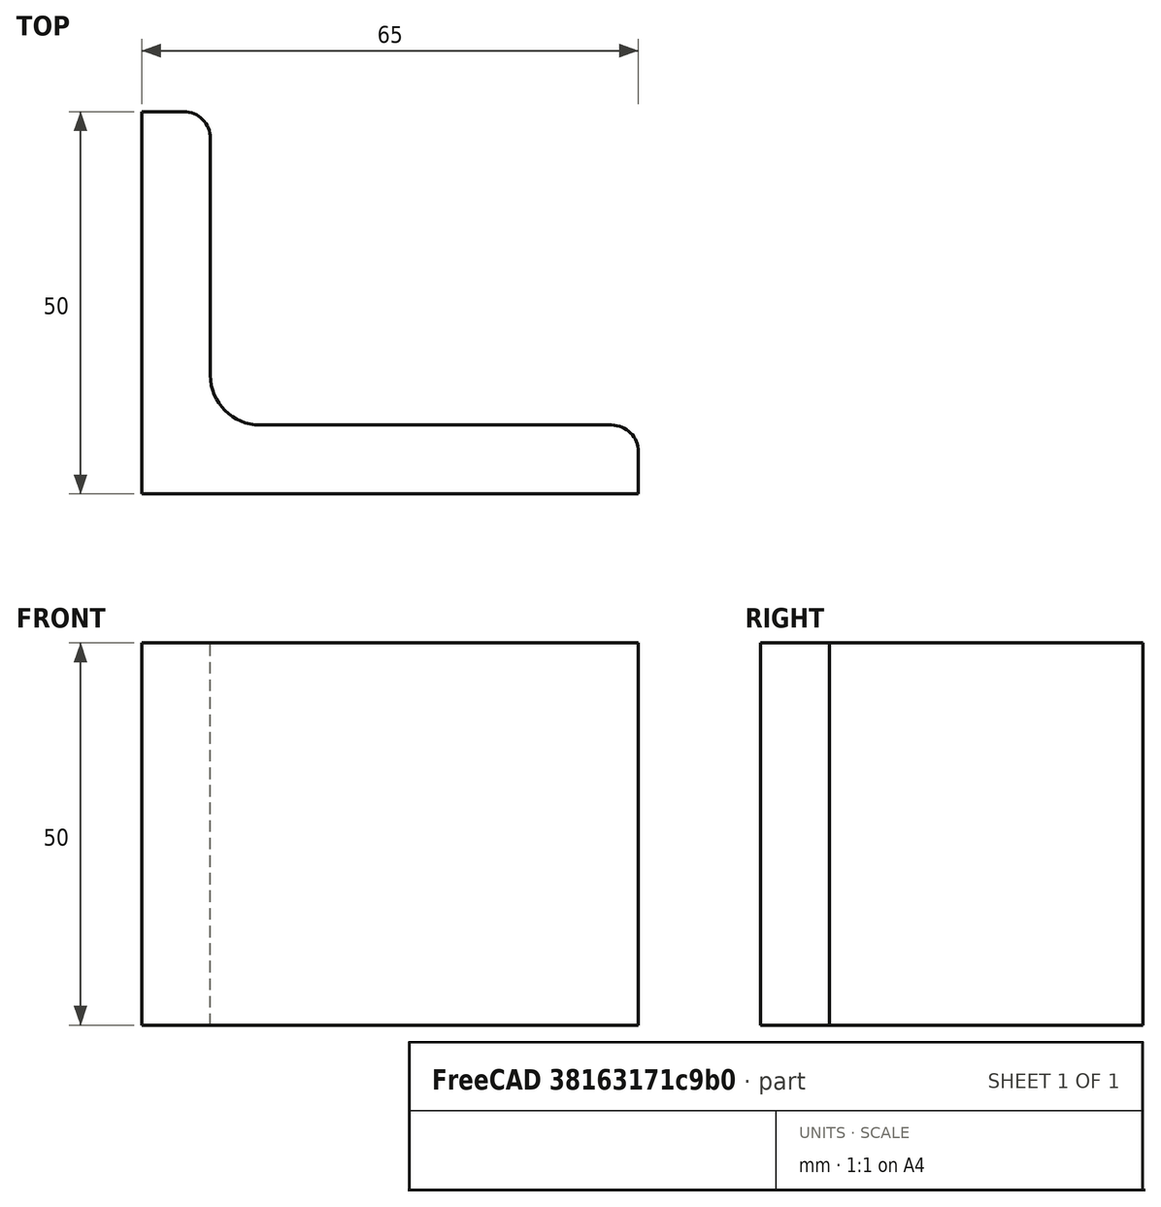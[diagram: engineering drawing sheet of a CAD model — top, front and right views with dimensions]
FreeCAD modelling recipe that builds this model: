
FCSTD DOCUMENT  (FreeCAD 0.15R4671 (Git))
Label: Angle Bar 65x50x9 EN10056 S235JR
License: All rights reserved
LicenseURL: http://en.wikipedia.org/wiki/All_rights_reserved
objects: Sketcher::SketchObject×1, Part::Extrusion×1
note: 2 computed .brp shape members not serialized (recipe doc carries the construction recipe); baked Part::Feature solids carry a one-line shape summary decoded from their .brp

FEATURE [Sketcher::SketchObject] Sketch
  sketch-geometry (9):
    g0: LineSegment StartX=0 StartY=0 StartZ=0 EndX=65 EndY=0 EndZ=0
    g1: LineSegment StartX=65 StartY=0 StartZ=0 EndX=65 EndY=5.5 EndZ=0
    g2: LineSegment StartX=61.5 StartY=9 StartZ=0 EndX=15.5 EndY=9 EndZ=0
    g3: LineSegment StartX=0 StartY=0 StartZ=0 EndX=0 EndY=50 EndZ=0
    g4: LineSegment StartX=0 StartY=50 StartZ=0 EndX=5.5 EndY=50 EndZ=0
    g5: LineSegment StartX=9 StartY=46.5 StartZ=0 EndX=9 EndY=15.5 EndZ=0
    g6: ArcOfCircle CenterX=15.5 CenterY=15.5 CenterZ=0 NormalX=0 NormalY=0 NormalZ=1 Radius=6.5 StartAngle=3.14159 EndAngle=4.71239
    g7: ArcOfCircle CenterX=5.5 CenterY=46.5 CenterZ=0 NormalX=0 NormalY=0 NormalZ=1 Radius=3.5 StartAngle=0 EndAngle=1.5708
    g8: ArcOfCircle CenterX=61.5 CenterY=5.5 CenterZ=0 NormalX=0 NormalY=0 NormalZ=1 Radius=3.5 StartAngle=0 EndAngle=1.5708
  constraints (23):
    c: Coincident(g0,g-1)
    c: Horizontal(g0)
    c: Coincident(g1,g0)
    c: Vertical(g1)
    c: Horizontal(g2)
    c: Coincident(g3,g-1)
    c: Vertical(g3)
    c: Coincident(g4,g3)
    c: Horizontal(g4)
    c: Vertical(g5)
    c: Tangent(g5,g6) = -1.5708
    c: Tangent(g2,g6) = 1.5708
    c: Tangent(g4,g7) = 1.5708
    c: Tangent(g5,g7) = 1.5708
    c: Tangent(g2,g8) = -1.5708
    c: Tangent(g1,g8) = -1.5708
    c: DistanceX(g0) = 65
    c: DistanceY(g3) = 50
    c: DistanceY(g0,g2) = 9
    c: DistanceX(g3,g5) = 9
    c: Radius(g6) = 6.5
    c: Radius(g8) = 3.5
    c: Radius(g7) = 3.5
FEATURE [Part::Extrusion] Extrude  label="Angle Bar 65x50x9 EN10056 S235JR"
  Base = -> Sketch
  Dir = (0,0,50)
  Solid = true
